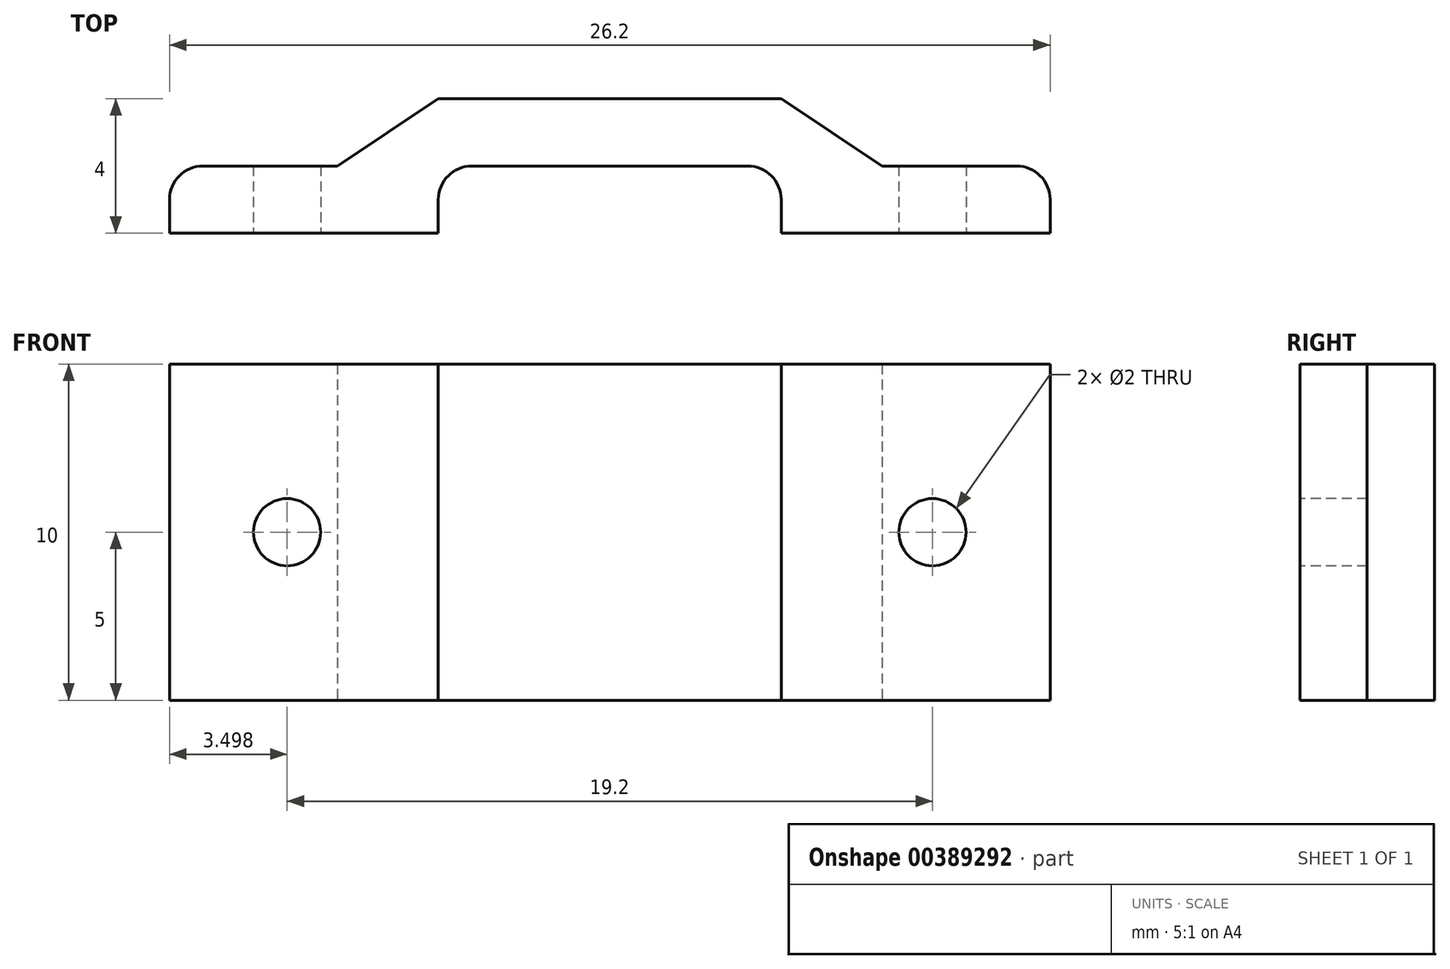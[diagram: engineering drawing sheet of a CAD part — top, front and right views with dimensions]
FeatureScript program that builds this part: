
annotation { "Feature Type Name" : "Feature", "Feature Type Description" : "" }
export const myFeature = defineFeature(function(context is Context, id is Id, definition is map)
    precondition{}
    {
        {
            var Q0;
            Q0=qCreatedBy(makeId("Top.planeOp"),FACE);
            var sketch = newSketch(context, id + "F0", { "sketchPlane" : qUnion([Q0])});
            skLineSegment(sketch, "E0", {"start": v(-31.71, 0) * mm, "end": v(-23.71, 0) * mm});
            skLineSegment(sketch, "E1", {"start": v(-23.71, 0) * mm, "end": v(-23.71, 1) * mm});
            skLineSegment(sketch, "E2", {"start": v(-22.71, 2) * mm, "end": v(-14.51, 2) * mm});
            skLineSegment(sketch, "E3", {"start": v(-13.51, 1) * mm, "end": v(-13.51, 0) * mm});
            skLineSegment(sketch, "E4", {"start": v(-13.51, 0) * mm, "end": v(-5.51, 0) * mm});
            skLineSegment(sketch, "E5", {"start": v(-23.71, 2) * mm, "end": v(-30.71, 2) * mm});
            skLineSegment(sketch, "E6", {"start": v(-31.71, 1) * mm, "end": v(-31.71, 0) * mm});
            skLineSegment(sketch, "E7", {"start": v(-13.51, 2) * mm, "end": v(-5.51, 2) * mm});
            skLineSegment(sketch, "E8", {"start": v(-6.51, 2) * mm, "end": v(-13.51, 2) * mm});
            skLineSegment(sketch, "E9", {"start": v(-23.71, 4) * mm, "end": v(-13.51, 4) * mm});
            skLineSegment(sketch, "E10", {"start": v(-13.51, 4) * mm, "end": v(-13.51, 2) * mm});
            skLineSegment(sketch, "E11", {"start": v(-23.71, 2) * mm, "end": v(-23.71, 4) * mm});
            skLineSegment(sketch, "E12", {"start": v(-5.51, 0) * mm, "end": v(-5.51, 1) * mm});
            skLineSegment(sketch, "E13", {"start": v(-23.71, 4) * mm, "end": v(-26.71, 2) * mm});
            skLineSegment(sketch, "E14", {"start": v(-13.51, 4) * mm, "end": v(-10.51, 2) * mm});
            skPoint(sketch, "E15.visualSharp", {"position": v(-31.71, 2) * mm});
            skArc(sketch, "E15.filletArc", {"start": v(-30.71, 2) * mm, "mid": v(-31.42, 1.7) * mm, "end": v(-31.71, 1) * mm});
            skPoint(sketch, "E16.visualSharp", {"position": v(-5.51, 2) * mm});
            skArc(sketch, "E16.filletArc", {"start": v(-5.51, 1) * mm, "mid": v(-5.8, 1.7) * mm, "end": v(-6.51, 2) * mm});
            skPoint(sketch, "E17.visualSharp", {"position": v(-23.71, 2) * mm});
            skArc(sketch, "E17.filletArc", {"start": v(-22.71, 2) * mm, "mid": v(-23.42, 1.7) * mm, "end": v(-23.71, 1) * mm});
            skPoint(sketch, "E18.visualSharp", {"position": v(-13.51, 2) * mm});
            skArc(sketch, "E18.filletArc", {"start": v(-13.51, 1) * mm, "mid": v(-13.8, 1.7) * mm, "end": v(-14.51, 2) * mm});
            skSolve(sketch);
        }
        {
            var Q0;
            Q0 = qSketchRegion(id + "F0", true);
            extrude(context, id + "F1", {"entities" : qUnion([Q0]), "depth" : 10 * mm, "offsetDistance" : 25 * mm});
        }
        {
            var Q0;
            Q0=makeQuery(id+"F1.opExtrude","SWEPT_FACE",FACE,{"disambiguationData":[OSD([sQuery(id+"F0.wireOp",EDGE,"E0")])]});
            var sketch = newSketch(context, id + "F2", { "sketchPlane" : qUnion([Q0])});
            skCircle(sketch, "E19", {"center": v(-28.21, 5) * mm, "radius": 1 * mm});
            skCircle(sketch, "E20", {"center": v(-9.01, 5) * mm, "radius": 1 * mm});
            skSolve(sketch);
        }
        {
            var Q0;
            Q0 = qSketchRegion(id + "F2", true);
            extrude(context, id + "F3", {"entities" : qUnion([Q0]), "operationType" : NewBodyOperationType.REMOVE, "endBound" : BoundingType.THROUGH_ALL, "oppositeDirection" : true, "depth" : 25 * mm, "offsetDistance" : 25 * mm});
        }
    });
